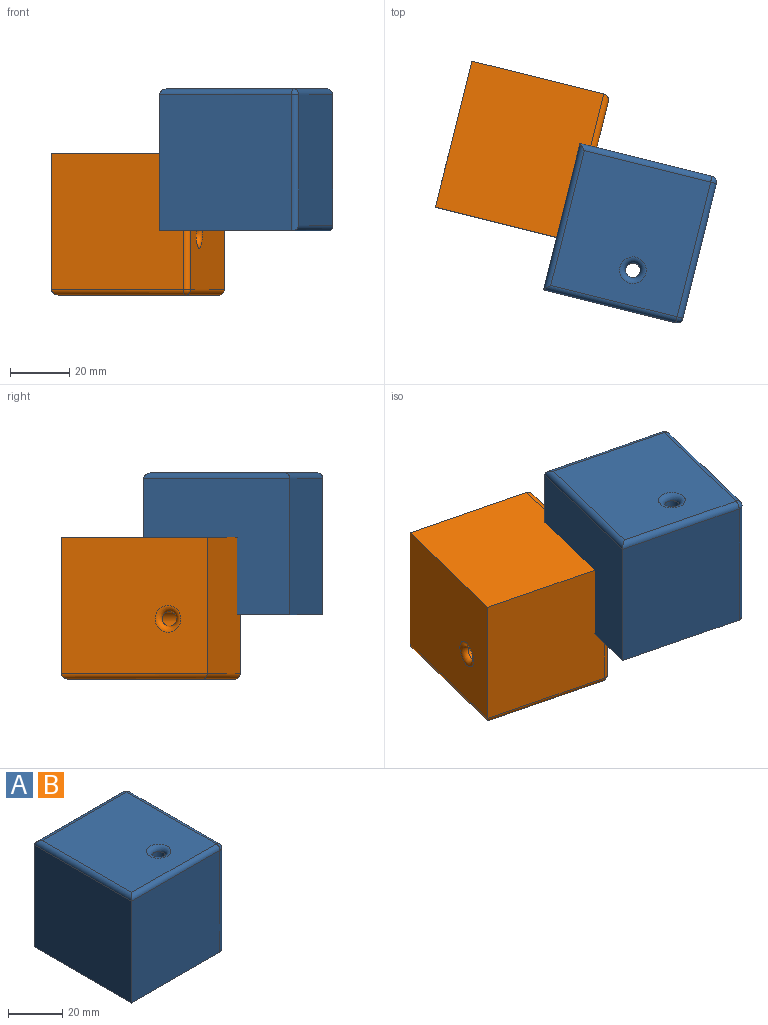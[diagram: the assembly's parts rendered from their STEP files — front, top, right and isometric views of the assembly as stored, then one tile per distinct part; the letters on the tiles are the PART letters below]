
ASSEMBLY  parts=2 mates=1
PART A: 18 faces, bbox 47.9x50.8x47.9 mm
  f0: plane 50.8x45.92mm, normal (-1,0,0), area 2332.5mm2, adj f1,f4,f5,f9
  f1: plane 50.8x45.92mm, normal (0,0,-1), area 2268.9mm2, adj f0,f4,f5,f7,f17
  f2: plane 46.8x43.92mm, normal (1,0,0), area 2055.2mm2, adj f11,f15,f16,f17
  f3: plane 46.8x43.92mm, normal (0,0,1), area 1991.6mm2, adj f8,f9,f10,f11,f12
  f4: plane 45.92x45.92mm, normal (0,-1,0), area 2108.2mm2, adj f0,f1,f10,f15
  f5: plane 45.92x45.92mm, normal (0,1,0), area 2108.2mm2, adj f0,f1,f12,f16
  f6: cylinder r=2.5mm len=43.92mm, axis (0,0,1), area 689.8mm2, adj f7,f8
  f7: torus R=4.5mm, axis (0,0,1), area 63.7mm2, adj f1,f6
  f8: torus R=4.5mm, axis (0,0,1), area 63.7mm2, adj f3,f6
  f9: cylinder r=2mm len=50.8mm, axis (0,1,0), area 155mm2, adj f0,f3,f10,f12
  f10: cylinder r=2mm len=45.92mm, axis (1,0,0), area 142mm2, adj f3,f4,f9,f13
  f11: cylinder r=2mm len=46.8mm, axis (0,-1,0), area 147mm2, adj f2,f3,f13,f14
  f12: cylinder r=2mm len=45.92mm, axis (-1,0,0), area 142mm2, adj f3,f5,f9,f14
  f13: sphere r=2mm, area 6.3mm2, adj f10,f11,f15
  f14: sphere r=2mm, area 6.3mm2, adj f11,f12,f16
  f15: cylinder r=2mm len=45.92mm, axis (0,0,-1), area 142mm2, adj f2,f4,f13,f17
  f16: cylinder r=2mm len=45.92mm, axis (0,0,1), area 142mm2, adj f2,f5,f14,f17
  f17: cylinder r=2mm len=50.8mm, axis (0,1,0), area 155mm2, adj f1,f2,f15,f16
PART B: same geometry as A
PLACE A rot(axis=(0,0,-1),14deg) t=(0,0,0)mm
PLACE B rot(axis=(0.12,0.99,-0.12),90.9deg) t=(-36.47,27.86,26.3)mm
MATE parallel B.f3 <-> A.f0  axis (0.97,-0.24,0) through (10.11,16.63,2.46)mm
